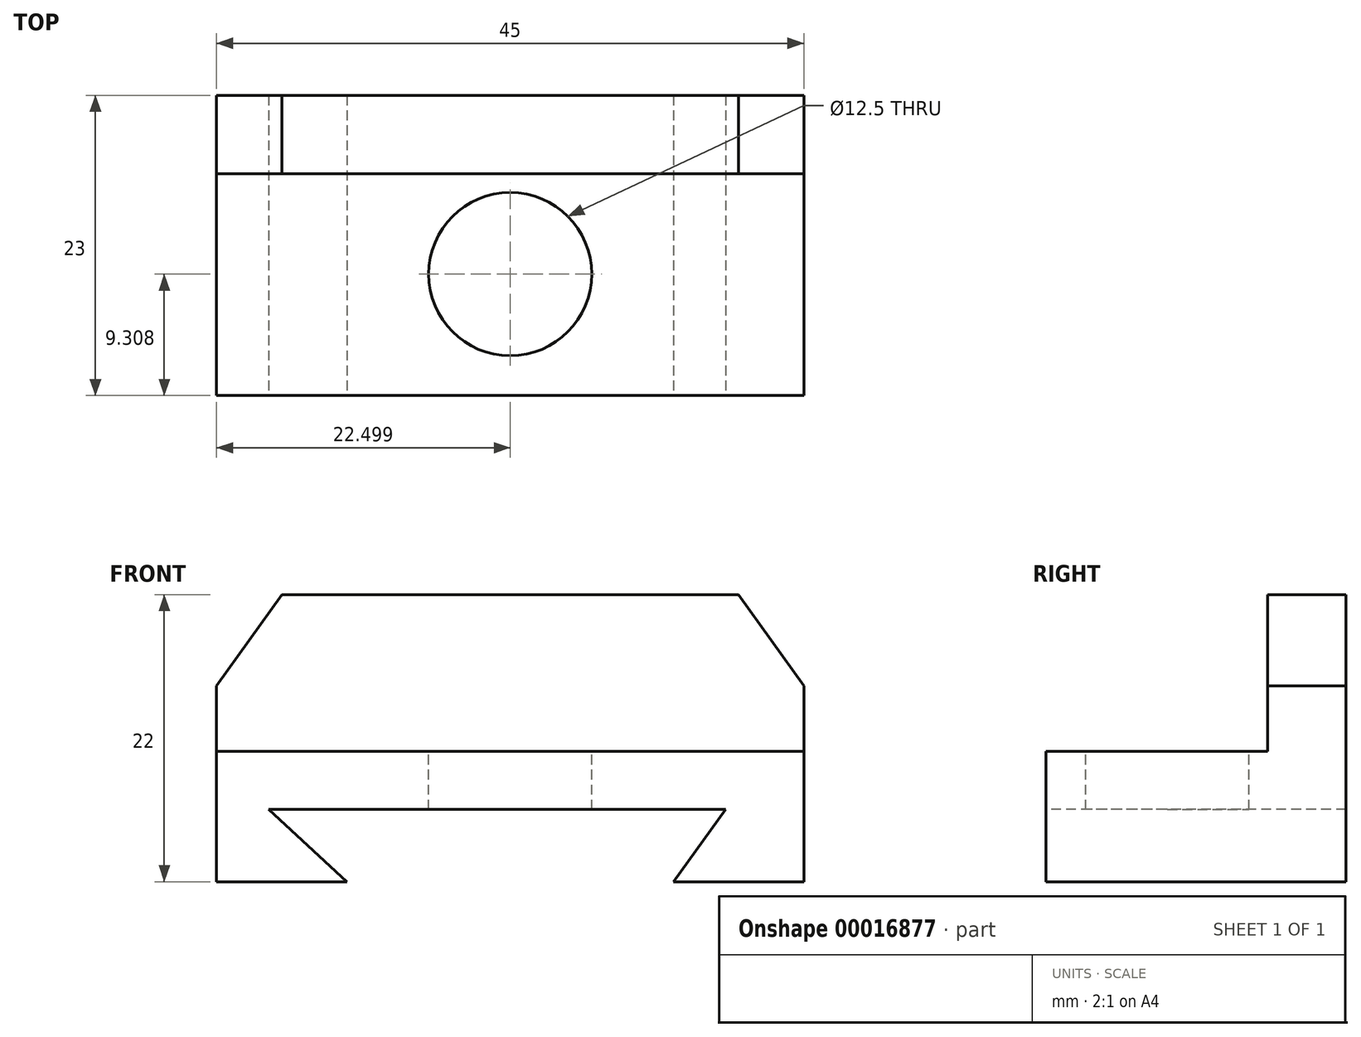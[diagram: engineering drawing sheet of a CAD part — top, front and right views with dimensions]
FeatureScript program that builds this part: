
annotation { "Feature Type Name" : "Feature", "Feature Type Description" : "" }
export const myFeature = defineFeature(function(context is Context, id is Id, definition is map)
    precondition{}
    {
        {
            var Q0;
            Q0=qCreatedBy(makeId("Top.planeOp"),FACE);
            var sketch = newSketch(context, id + "F0", { "sketchPlane" : qUnion([Q0])});
            skLineSegment(sketch, "E0.bottom", {"start": v(-13.76, -2.91) * mm, "end": v(31.24, -2.91) * mm});
            skLineSegment(sketch, "E0.top", {"start": v(-13.76, -25.91) * mm, "end": v(31.24, -25.91) * mm});
            skLineSegment(sketch, "E0.left", {"start": v(-13.76, -2.91) * mm, "end": v(-13.76, -25.91) * mm});
            skLineSegment(sketch, "E0.right", {"start": v(31.24, -2.91) * mm, "end": v(31.24, -25.91) * mm});
            skLineSegment(sketch, "E1", {"start": v(-13.76, -8.91) * mm, "end": v(31.24, -8.91) * mm});
            skCircle(sketch, "E2", {"center": v(8.74, -16.6) * mm, "radius": 6.25 * mm});
            skSolve(sketch);
        }
        {
            var Q0;
            {var subQ2=sQuery(id+"F0.wireOp",EDGE,"E0.top");Q0=makeQuery(id+"F0.imprint","IMPRINT",FACE,{"disambiguationData":[TD([[makeQuery(id+"F0.imprint","IMPRINT",EDGE,{"derivedFrom":subQ2}),1.0]])]});}
            var Q1;
            {var subQ2=sQuery(id+"F0.wireOp",EDGE,"E0.bottom");Q1=makeQuery(id+"F0.imprint","IMPRINT",FACE,{"disambiguationData":[TD([[makeQuery(id+"F0.imprint","IMPRINT",EDGE,{"derivedFrom":subQ2}),-1.0]])]});}
            var Q2;
            Q2=makeQuery(id+"F0.imprint","IMPRINT",FACE,{"disambiguationData":[TD([[makeQuery(id+"F0.imprint","IMPRINT",EDGE,{"derivedFrom":sQuery(id+"F0.wireOp",EDGE,"E2")}),1.0]])]});
            extrude(context, id + "F1", {"entities" : qUnion([Q0, Q1, Q2]), "oppositeDirection" : true, "depth" : 10 * mm});
        }
        {
            var Q0;
            Q0=makeQuery(id+"F0.imprint","IMPRINT",FACE,{"disambiguationData":[TD([[makeQuery(id+"F0.imprint","IMPRINT",EDGE,{"derivedFrom":sQuery(id+"F0.wireOp",EDGE,"E2")}),1.0]])]});
            extrude(context, id + "F2", {"entities" : qUnion([Q0]), "operationType" : NewBodyOperationType.REMOVE, "oppositeDirection" : true, "depth" : 25 * mm});
        }
        {
            var Q0;
            {var subQ2=sQuery(id+"F0.wireOp",EDGE,"E0.bottom");Q0=makeQuery(id+"F0.imprint","IMPRINT",FACE,{"disambiguationData":[TD([[makeQuery(id+"F0.imprint","IMPRINT",EDGE,{"derivedFrom":subQ2}),-1.0]])]});}
            extrude(context, id + "F3", {"entities" : qUnion([Q0]), "operationType" : NewBodyOperationType.ADD, "depth" : 12 * mm});
        }
        {
            var Q0;
            Q0=makeQuery(id+"F3.opExtrude","SWEPT_FACE",FACE,{"disambiguationData":[OSD([sQuery(id+"F0.wireOp",EDGE,"E1")])]});
            var sketch = newSketch(context, id + "F4", { "sketchPlane" : qUnion([Q0])});
            skLineSegment(sketch, "E3", {"start": v(-8.76, 12) * mm, "end": v(-13.76, 5) * mm});
            skLineSegment(sketch, "E4", {"start": v(26.24, 12) * mm, "end": v(31.24, 5) * mm});
            skSolve(sketch);
        }
        {
            var Q0;
            {var subQ2=sQuery(id+"F4.wireOp",EDGE,"E3");Q0=makeQuery(id+"F4.imprint","IMPRINT",FACE,{"disambiguationData":[TD([[makeQuery(id+"F4.imprint","IMPRINT",EDGE,{"derivedFrom":subQ2}),-1.0]])]});}
            extrude(context, id + "F5", {"entities" : qUnion([Q0]), "operationType" : NewBodyOperationType.REMOVE, "oppositeDirection" : true, "depth" : 25 * mm});
        }
        {
            var Q0;
            {var subQ2=sQuery(id+"F4.wireOp",EDGE,"E4");Q0=makeQuery(id+"F4.imprint","IMPRINT",FACE,{"disambiguationData":[TD([[makeQuery(id+"F4.imprint","IMPRINT",EDGE,{"derivedFrom":subQ2}),1.0]])]});}
            extrude(context, id + "F6", {"entities" : qUnion([Q0]), "operationType" : NewBodyOperationType.REMOVE, "oppositeDirection" : true, "depth" : 25 * mm});
        }
        {
            var Q0;
            Q0=makeQuery(id+"F1.opExtrude","SWEPT_FACE",FACE,{"disambiguationData":[OSD([sQuery(id+"F0.wireOp",EDGE,"E0.top")])]});
            var sketch = newSketch(context, id + "F7", { "sketchPlane" : qUnion([Q0])});
            skLineSegment(sketch, "E5", {"start": v(-3.76, -10) * mm, "end": v(-9.76, -4.47) * mm});
            skLineSegment(sketch, "E6", {"start": v(-9.76, -4.47) * mm, "end": v(25.24, -4.47) * mm});
            skLineSegment(sketch, "E7", {"start": v(25.24, -4.47) * mm, "end": v(21.24, -10) * mm});
            skSolve(sketch);
        }
        {
            var Q0;
            {var subQ2=sQuery(id+"F7.wireOp",EDGE,"E5");Q0=makeQuery(id+"F7.imprint","IMPRINT",FACE,{"disambiguationData":[TD([[makeQuery(id+"F7.imprint","IMPRINT",EDGE,{"derivedFrom":subQ2}),-1.0]])]});}
            extrude(context, id + "F8", {"entities" : qUnion([Q0]), "operationType" : NewBodyOperationType.REMOVE, "oppositeDirection" : true, "depth" : 25 * mm});
        }
    });
